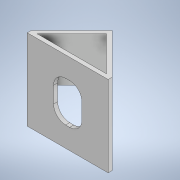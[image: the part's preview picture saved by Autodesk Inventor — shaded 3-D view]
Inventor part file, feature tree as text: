
AUTODESK INVENTOR PART (.ipt)
format: ipt  version: 2020 (Build 240168000, 168)  size: 133,120 bytes
history: native  units: mm
features: extrude x3, sketch x3
ambient origin geometry x8: Origin, YZ Plane, XZ Plane, XY Plane, X Axis, Y Axis, Z Axis, Center Point
bodies: Solid1 (feature_tree)
feature tree (6):
  extrude  "Extrusion1"  Depth=100.0mm
  extrude  "Extrusion2"  TaperAngle=45.0deg  [1 undecoded]
  extrude  "Extrusion3"  Depth=5.0mm
  sketch  "Sketch1"  dims[d0=100.0mm d1=100.0mm]
  sketch  "Sketch2"  dims[d2=5.0mm d3=0.0mm d4=45.0deg]
  sketch  "Sketch3"  dims[d5=5.0mm d6=5.0mm d7=55.0mm d8=0.0mm d9=35.0mm d10=50.0mm d11=15.0mm d12=5.0mm d13=0.0mm]
note: 1 required parameter value undecoded (feature->parameter linkage not recoverable at this tier; creation-order binding heuristic only, values carry confidence <= 0.55)
